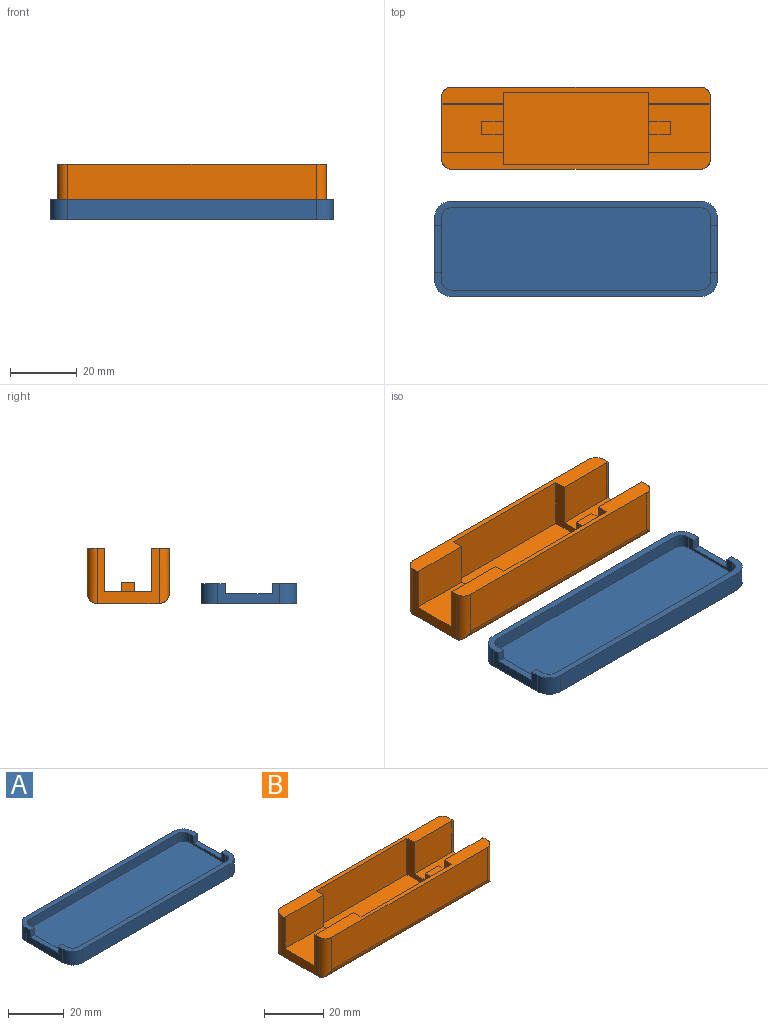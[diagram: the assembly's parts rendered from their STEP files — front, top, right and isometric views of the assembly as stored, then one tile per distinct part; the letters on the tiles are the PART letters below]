
ASSEMBLY  parts=2 mates=1
PART A: 97 faces, bbox 84.6x28.6x6 mm
  f0: plane 84.62x28.64mm, normal (0,0,-1), area 2153.2mm2, adj f1,f3,f4,f5,f6,f7,f8,f9
  f1: plane 18.64x6mm, normal (1,0,0), area 69.8mm2, adj f0,f2,f4,f5,f10,f23,f24,f25
  f2: plane 84.62x7.32mm, normal (0,0,1), area 183.6mm2, adj f1,f5,f6,f7,f8,f13,f14,f15
  f3: plane 74.62x6mm, normal (0,-1,0), area 447.7mm2, adj f0,f4,f9,f10
  f4: cylinder r=5mm len=6mm, axis (0,0,-1), area 47.1mm2, adj f0,f1,f3,f10
  f5: cylinder r=5mm len=6mm, axis (0,0,-1), area 47.1mm2, adj f0,f1,f2,f6
  f6: plane 74.62x6mm, normal (0,1,0), area 447.7mm2, adj f0,f2,f5,f7
  f7: cylinder r=5mm len=6mm, axis (0,0,-1), area 47.1mm2, adj f0,f2,f6,f8
  f8: plane 18.64x6mm, normal (-1,0,0), area 69.8mm2, adj f0,f2,f7,f9,f10,f20,f21,f22
  f9: cylinder r=5mm len=6mm, axis (0,0,-1), area 47.1mm2, adj f0,f3,f8,f10
  f10: plane 84.62x7.32mm, normal (0,0,1), area 183.6mm2, adj f1,f3,f4,f8,f9,f11,f12,f13
  f11: plane 74.62x4mm, normal (0,1,0), area 298.5mm2, adj f10,f12,f18,f19
  f12: cylinder r=3mm len=4mm, axis (0,0,-1), area 18.8mm2, adj f10,f11,f13,f19
  f13: plane 18.64x4mm, normal (-1,0,0), area 32.6mm2, adj f2,f10,f12,f14,f19,f23,f24,f25
  f14: cylinder r=3mm len=4mm, axis (0,0,-1), area 18.8mm2, adj f2,f13,f15,f19
  f15: plane 74.62x4mm, normal (0,-1,0), area 298.5mm2, adj f2,f14,f16,f19
  f16: cylinder r=3mm len=4mm, axis (0,0,-1), area 18.8mm2, adj f2,f15,f17,f19
  f17: plane 18.64x4mm, normal (1,0,0), area 32.6mm2, adj f2,f10,f16,f18,f19,f20,f21,f22
  f18: cylinder r=3mm len=4mm, axis (0,0,-1), area 18.8mm2, adj f10,f11,f17,f19
  f19: plane 80.62x24.64mm, normal (0,0,1), area 1978.8mm2, adj f11,f12,f13,f14,f15,f16,f17,f18
  f20: plane 3x2mm, normal (0,-1,0), area 6mm2, adj f2,f8,f17,f21
  f21: plane 14x2mm, normal (0,0,1), area 28mm2, adj f8,f17,f20,f22
  f22: plane 3x2mm, normal (0,1,0), area 6mm2, adj f8,f10,f17,f21
  f23: plane 3x2mm, normal (0,1,0), area 6mm2, adj f1,f10,f13,f24
  f24: plane 14x2mm, normal (0,0,1), area 28mm2, adj f1,f13,f23,f25
  f25: plane 3x2mm, normal (0,-1,0), area 6mm2, adj f1,f2,f13,f24
  f26: plane 4.53x0.5mm, normal (1,0,0), area 2.3mm2, adj f0,f27,f32,f33
  f27: plane 15.31x0.5mm, normal (0,-1,0), area 7.7mm2, adj f0,f26,f28,f33
  f28: plane 2.94x0.5mm, normal (0.99,0.11,0), area 1.5mm2, adj f0,f27,f29,f33
  f29: plane 9.86x5.21mm, normal (-0.47,-0.88,0), area 5.6mm2, adj f0,f28,f30,f33
  f30: plane 9.86x5.21mm, normal (-0.47,0.88,0), area 5.6mm2, adj f0,f29,f31,f33
  f31: plane 2.94x0.5mm, normal (0.99,-0.11,0), area 1.5mm2, adj f0,f30,f32,f33
  f32: plane 15.31x0.5mm, normal (0,1,0), area 7.7mm2, adj f0,f26,f31,f33
  f33: plane 24.85x10.41mm, normal (0,0,-1), area 118.3mm2, adj f26,f27,f28,f29,f30,f31,f32
  f34: plane 1.03x0.5mm, normal (0,-1,0), area 0.5mm2, adj f0,f35,f41,f42
  f35: plane 7.93x0.5mm, normal (-1,0,0), area 4mm2, adj f0,f34,f36,f42
  f36: plane 2.8x0.5mm, normal (0,-1,0), area 1.4mm2, adj f0,f35,f37,f42
  f37: plane 0.91x0.5mm, normal (-1,0,0), area 0.5mm2, adj f0,f36,f38,f42
  f38: plane 6.63x0.5mm, normal (0,1,0), area 3.3mm2, adj f0,f37,f39,f42
  f39: plane 0.91x0.5mm, normal (1,0,0), area 0.5mm2, adj f0,f38,f40,f42
  f40: plane 2.8x0.5mm, normal (0,-1,0), area 1.4mm2, adj f0,f39,f41,f42
  f41: plane 7.93x0.5mm, normal (1,0,0), area 4mm2, adj f0,f34,f40,f42
  f42: plane 8.85x6.63mm, normal (0,0,-1), area 14.2mm2, adj f34,f35,f36,f37,f38,f39,f40,f41
  f43: plane 5.73x0.5mm, normal (-1,0,0), area 2.9mm2, adj f0,f44,f56,f57
  f44: plane 1.03x0.5mm, normal (0,1,0), area 0.5mm2, adj f0,f43,f45,f57
  f45: plane 5.76x0.5mm, normal (1,0,0), area 2.9mm2, adj f0,f44,f46,f57
  f46: extruded ~1.71x0.61mm, area 0.9mm2, adj f0,f45,f47,f57
  f47: extruded ~1.72x0.6mm, area 0.9mm2, adj f0,f46,f48,f57
  f48: extruded ~1.78x0.59mm, area 1mm2, adj f0,f47,f49,f57
  f49: extruded ~1.7x0.61mm, area 0.9mm2, adj f0,f48,f50,f57
  f50: plane 5.77x0.5mm, normal (-1,0,0), area 2.9mm2, adj f0,f49,f51,f57
  f51: plane 1.03x0.5mm, normal (0,1,0), area 0.5mm2, adj f0,f50,f52,f57
  f52: plane 5.7x0.5mm, normal (1,0,0), area 2.9mm2, adj f0,f51,f53,f57
  f53: extruded ~2.4x0.87mm, area 1.3mm2, adj f0,f52,f54,f57
  f54: extruded ~2.47x0.87mm, area 1.3mm2, adj f0,f53,f55,f57
  f55: extruded ~2.51x0.87mm, area 1.4mm2, adj f0,f54,f56,f57
  f56: extruded ~2.38x0.91mm, area 1.3mm2, adj f0,f43,f55,f57
  f57: plane 8.97x6.77mm, normal (0,0,-1), area 20.6mm2, adj f43,f44,f45,f46,f47,f48,f49,f50
  f58: plane 1.17x0.5mm, normal (0,-1,0), area 0.6mm2, adj f0,f59,f72,f73
  f59: plane 8.85x0.5mm, normal (-1,0,0), area 4.4mm2, adj f0,f58,f60,f73
  f60: plane 0.96x0.5mm, normal (0,1,0), area 0.5mm2, adj f0,f59,f61,f73
  f61: plane 5.08x0.5mm, normal (1,0,0), area 2.5mm2, adj f0,f60,f62,f73
  f62: extruded ~1.27x0.5mm, area 0.6mm2, adj f0,f61,f63,f73
  f63: extruded ~1.05x0.5mm, area 0.5mm2, adj f0,f62,f64,f73
  f64: plane 0.5x0.05mm, normal (0,1,0), area 0mm2, adj f0,f63,f65,f73
  f65: plane 7.4x4.82mm, normal (-0.84,0.55,0), area 4.4mm2, adj f0,f64,f66,f73
  f66: plane 1.16x0.5mm, normal (0,1,0), area 0.6mm2, adj f0,f65,f67,f73
  f67: plane 8.85x0.5mm, normal (1,0,0), area 4.4mm2, adj f0,f66,f68,f73
  f68: plane 0.95x0.5mm, normal (0,-1,0), area 0.5mm2, adj f0,f67,f69,f73
  f69: plane 5.03x0.5mm, normal (-1,0,0), area 2.5mm2, adj f0,f68,f70,f73
  f70: extruded ~2.4x0.5mm, area 1.2mm2, adj f0,f69,f71,f73
  f71: plane 0.5x0.05mm, normal (0,-1,0), area 0mm2, adj f0,f70,f72,f73
  f72: plane 7.43x4.84mm, normal (0.84,-0.55,0), area 4.4mm2, adj f0,f58,f71,f73
  f73: plane 8.85x6.91mm, normal (0,0,-1), area 25.8mm2, adj f58,f59,f60,f61,f62,f63,f64,f65
  f74: extruded ~2.73x0.77mm, area 1.4mm2, adj f75,f89,f90,f96
  f75: extruded ~2.7x0.77mm, area 1.4mm2, adj f74,f76,f90,f96
  f76: extruded ~2.24x0.93mm, area 1.3mm2, adj f75,f77,f90,f96
  f77: extruded ~2.21x0.92mm, area 1.2mm2, adj f76,f78,f90,f96
  f78: extruded ~2.71x0.75mm, area 1.4mm2, adj f77,f79,f90,f96
  f79: extruded ~2.73x0.75mm, area 1.4mm2, adj f78,f80,f90,f96
  f80: extruded ~2.22x0.93mm, area 1.2mm2, adj f79,f89,f90,f96
  f81: extruded ~3.34x1.08mm, area 1.8mm2, adj f0,f82,f88,f90
  f82: extruded ~3.34x1.07mm, area 1.8mm2, adj f0,f81,f83,f90
  f83: extruded ~2.98x1.21mm, area 1.7mm2, adj f0,f82,f84,f90
  f84: extruded ~3.03x1.19mm, area 1.7mm2, adj f0,f83,f85,f90
  f85: extruded ~3.35x1.07mm, area 1.8mm2, adj f0,f84,f86,f90
  f86: extruded ~3.37x1.06mm, area 1.8mm2, adj f0,f85,f87,f90
  f87: extruded ~3.02x1.2mm, area 1.7mm2, adj f0,f86,f88,f90
  f88: extruded ~2.99x1.22mm, area 1.7mm2, adj f0,f81,f87,f90
  f89: extruded ~2.22x0.93mm, area 1.2mm2, adj f74,f80,f90,f96
  f90: plane 9.11x8.14mm, normal (0,0,-1), area 24.8mm2, adj f74,f75,f76,f77,f78,f79,f80,f81
  f91: plane 8.85x0.5mm, normal (1,0,0), area 4.4mm2, adj f0,f92,f94,f95
  f92: plane 1.03x0.5mm, normal (0,-1,0), area 0.5mm2, adj f0,f91,f93,f95
  f93: plane 8.85x0.5mm, normal (-1,0,0), area 4.4mm2, adj f0,f92,f94,f95
  f94: plane 1.03x0.5mm, normal (0,1,0), area 0.5mm2, adj f0,f91,f93,f95
  f95: plane 8.85x1.03mm, normal (0,0,-1), area 9.1mm2, adj f91,f92,f93,f94
  f96: plane 7.29x5.96mm, normal (0,0,-1), area 36mm2, adj f74,f75,f76,f77,f78,f79,f80,f89
PART B: 36 faces, bbox 80.5x24.5x16.5 mm
  f0: plane 4x2.8mm, normal (1,0,0), area 11.2mm2, adj f23,f25,f26,f34
  f1: plane 80.5x5.3mm, normal (0,0,1), area 246.5mm2, adj f3,f4,f6,f8,f10,f12,f16,f17
  f2: plane 80.5x5.3mm, normal (0,0,1), area 246.5mm2, adj f3,f4,f5,f8,f9,f12,f18,f19
  f3: plane 21.5x15mm, normal (-1,0,0), area 145.2mm2, adj f1,f2,f9,f10,f11,f23,f24,f25
  f4: plane 18.5x16.5mm, normal (1,0,0), area 124.4mm2, adj f1,f2,f7,f21,f22,f23,f28,f31
  f5: plane 74.5x13.5mm, normal (0,-1,0), area 1005.7mm2, adj f2,f28,f29,f30
  f6: plane 74.5x13.5mm, normal (0,1,0), area 1005.7mm2, adj f1,f31,f32,f33
  f7: plane 80.5x18.5mm, normal (0,0,-1), area 1489.2mm2, adj f4,f12,f29,f32
  f8: plane 21.5x15mm, normal (1,0,0), area 145.2mm2, adj f1,f2,f9,f10,f11,f13,f15,f16
  f9: plane 43.5x15mm, normal (0,1,0), area 652.5mm2, adj f2,f3,f8,f11
  f10: plane 43.5x15mm, normal (0,-1,0), area 652.5mm2, adj f1,f3,f8,f11
  f11: plane 43.5x21.5mm, normal (0,0,1), area 935.2mm2, adj f3,f8,f9,f10
  f12: plane 18.5x16.5mm, normal (-1,0,0), area 124.4mm2, adj f1,f2,f7,f17,f18,f20,f30,f33
  f13: plane 6.5x2.8mm, normal (0,-1,0), area 18.2mm2, adj f8,f14,f20,f35
  f14: plane 4x2.8mm, normal (-1,0,0), area 11.2mm2, adj f13,f15,f20,f35
  f15: plane 6.5x2.8mm, normal (0,1,0), area 18.2mm2, adj f8,f14,f20,f35
  f16: plane 18x13mm, normal (0,-1,0), area 234mm2, adj f1,f8,f17,f20
  f17: plane 13x0.5mm, normal (0.51,-0.86,0), area 7.6mm2, adj f1,f12,f16,f20
  f18: plane 13x0.5mm, normal (0.51,0.86,0), area 7.6mm2, adj f2,f12,f19,f20
  f19: plane 18x13mm, normal (0,1,0), area 234mm2, adj f2,f8,f18,f20
  f20: plane 18.5x14.5mm, normal (0,0,1), area 242.1mm2, adj f8,f12,f13,f14,f15,f16,f17,f18
  f21: plane 13x0.5mm, normal (-0.51,-0.86,0), area 7.6mm2, adj f1,f4,f23,f24
  f22: plane 13x0.5mm, normal (-0.51,0.86,0), area 7.6mm2, adj f2,f4,f23,f27
  f23: plane 18.5x14.5mm, normal (0,0,1), area 242.1mm2, adj f0,f3,f4,f21,f22,f24,f25,f26
  f24: plane 18x13mm, normal (0,-1,0), area 234mm2, adj f1,f3,f21,f23
  f25: plane 6.5x2.8mm, normal (0,1,0), area 18.2mm2, adj f0,f3,f23,f34
  f26: plane 6.5x2.8mm, normal (0,-1,0), area 18.2mm2, adj f0,f3,f23,f34
  f27: plane 18x13mm, normal (0,1,0), area 234mm2, adj f2,f3,f22,f23
  f28: cylinder r=3mm len=16.5mm, axis (0,0,-1), area 72.6mm2, adj f2,f4,f5,f29
  f29: cylinder r=3mm len=80.5mm, axis (1,0,0), area 369.1mm2, adj f5,f7,f28,f30
  f30: cylinder r=3mm len=16.5mm, axis (0,0,1), area 72.6mm2, adj f2,f5,f12,f29
  f31: cylinder r=3mm len=16.5mm, axis (0,0,1), area 72.6mm2, adj f1,f4,f6,f32
  f32: cylinder r=3mm len=80.5mm, axis (-1,0,0), area 369.1mm2, adj f6,f7,f31,f33
  f33: cylinder r=3mm len=16.5mm, axis (0,0,-1), area 72.6mm2, adj f1,f6,f12,f32
  f34: plane 6.5x4mm, normal (0,0,1), area 26mm2, adj f0,f3,f25,f26
  f35: plane 6.5x4mm, normal (0,0,1), area 26mm2, adj f8,f13,f14,f15
PLACE A t=(-0.06,-36.17,-20.5)mm
PLACE B at identity
MATE planar A.f0 <-> B.f7  axis (0,0,-1) through (-19.09,-45.31,-1.5)mm
